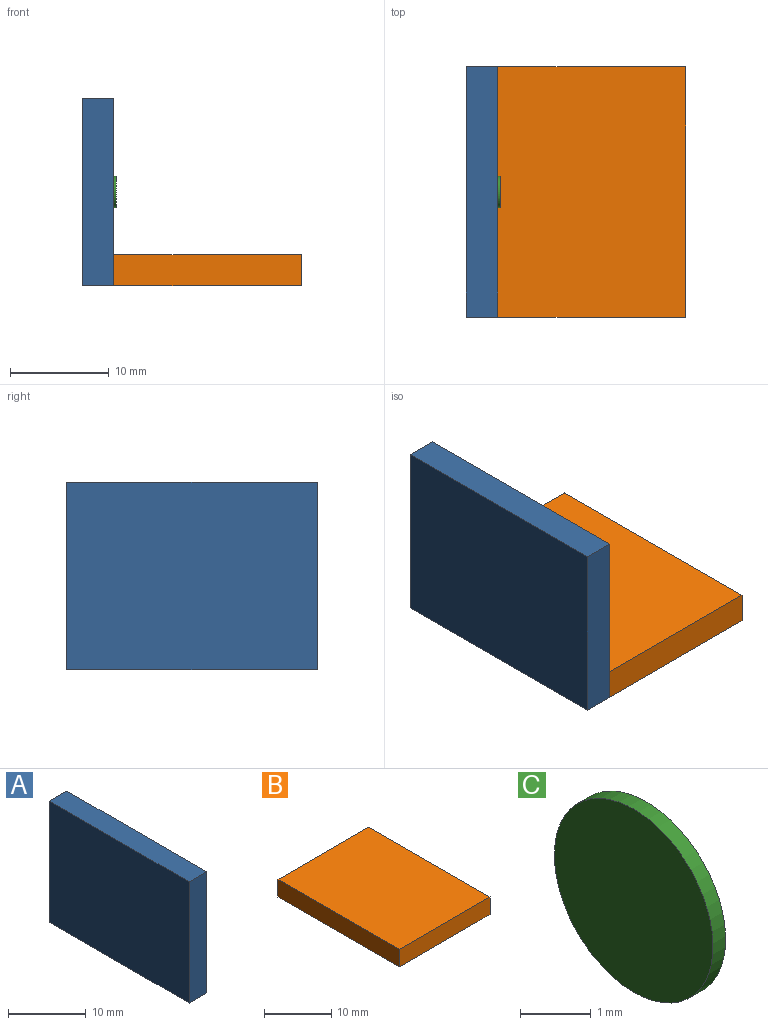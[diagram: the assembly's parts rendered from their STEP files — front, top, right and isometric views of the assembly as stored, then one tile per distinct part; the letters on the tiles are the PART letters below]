
ASSEMBLY  parts=3 mates=2
PART A: 6 faces, bbox 3.2x25.4x19.1 mm
  f0: plane 19.05x3.18mm, normal (0,-1,0), area 60.5mm2, adj f1,f3,f4,f5
  f1: plane 25.4x3.18mm, normal (0,0,-1), area 80.6mm2, adj f0,f2,f4,f5
  f2: plane 19.05x3.18mm, normal (0,1,0), area 60.5mm2, adj f1,f3,f4,f5
  f3: plane 25.4x3.18mm, normal (0,0,1), area 80.6mm2, adj f0,f2,f4,f5
  f4: plane 25.4x19.05mm, normal (1,0,0), area 483.9mm2, adj f0,f1,f2,f3
  f5: plane 25.4x19.05mm, normal (-1,0,0), area 483.9mm2, adj f0,f1,f2,f3
PART B: 6 faces, bbox 19.1x25.4x3.2 mm
  f0: plane 25.4x19.05mm, normal (0,0,1), area 483.9mm2, adj f1,f3,f4,f5
  f1: plane 19.05x3.18mm, normal (0,-1,0), area 60.5mm2, adj f0,f2,f4,f5
  f2: plane 25.4x19.05mm, normal (0,0,-1), area 483.9mm2, adj f1,f3,f4,f5
  f3: plane 19.05x3.18mm, normal (0,1,0), area 60.5mm2, adj f0,f2,f4,f5
  f4: plane 25.4x3.18mm, normal (1,0,0), area 80.6mm2, adj f0,f1,f2,f3
  f5: plane 25.4x3.18mm, normal (-1,0,0), area 80.6mm2, adj f0,f1,f2,f3
PART C: 3 faces, bbox 0.3x3.2x3.2 mm
  f0: cylinder r=1.59mm len=3.18mm, axis (-1,0,0), area 2.5mm2, adj f1,f2
  f1: plane 3.18x3.18mm, normal (1,0,0), area 7.9mm2, adj f0
  f2: plane 3.18x3.18mm, normal (-1,0,0), area 7.9mm2, adj f0
PLACE A at identity
PLACE B at identity
PLACE C rot(axis=(0,1,0),180deg) t=(133.6,0,6.35)mm
MATE fastened B.f5 <-> A.f4  axis (-1,0,0) through (66.68,-12.7,-6.35)mm
MATE fastened C.f0 <-> A.f4  axis (-1,0,0) through (66.68,0,3.18)mm
